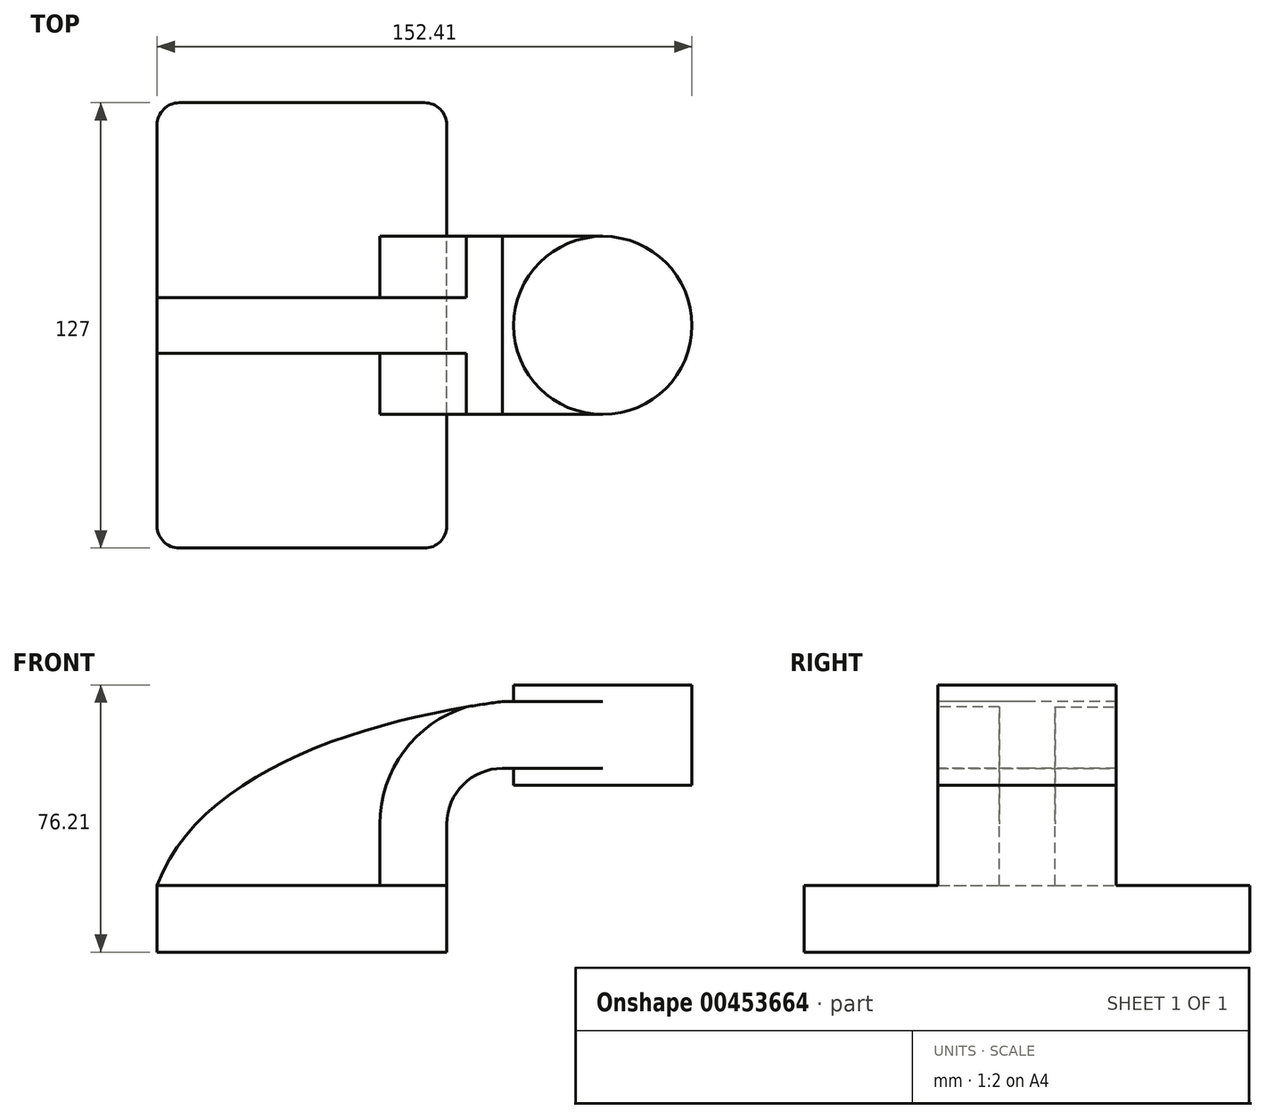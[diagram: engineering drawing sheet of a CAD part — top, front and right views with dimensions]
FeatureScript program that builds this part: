
annotation { "Feature Type Name" : "Feature", "Feature Type Description" : "" }
export const myFeature = defineFeature(function(context is Context, id is Id, definition is map)
    precondition{}
    {
        {
            var Q0;
            Q0=qCreatedBy(makeId("Front.planeOp"),FACE);
            var sketch = newSketch(context, id + "F0", { "sketchPlane" : qUnion([Q0])});
            skLineSegment(sketch, "E0.bottom", {"start": v(41.27, 9.53) * mm, "end": v(-41.28, 9.53) * mm});
            skLineSegment(sketch, "E0.top", {"start": v(41.28, -9.52) * mm, "end": v(-41.27, -9.52) * mm});
            skLineSegment(sketch, "E0.left", {"start": v(41.28, 9.53) * mm, "end": v(41.28, -9.52) * mm});
            skLineSegment(sketch, "E0.right", {"start": v(-41.28, 9.53) * mm, "end": v(-41.27, -9.52) * mm});
            skPoint(sketch, "E0.middle", {"position": v(0, 0) * mm});
            skLineSegment(sketch, "E1.bottom", {"start": v(111.13, 38.1) * mm, "end": v(60.32, 38.1) * mm});
            skLineSegment(sketch, "E1.top", {"start": v(111.13, 66.68) * mm, "end": v(60.33, 66.68) * mm});
            skLineSegment(sketch, "E1.left", {"start": v(111.13, 38.1) * mm, "end": v(111.13, 66.68) * mm});
            skLineSegment(sketch, "E1.right", {"start": v(60.33, 38.1) * mm, "end": v(60.33, 66.68) * mm});
            skPoint(sketch, "E1.middle", {"position": v(85.73, 52.39) * mm});
            skLineSegment(sketch, "E2", {"start": v(41.27, 9.53) * mm, "end": v(41.27, 27) * mm});
            skArc(sketch, "E3", {"start": v(41.27, 27) * mm, "mid": v(45.92, 38.23) * mm, "end": v(57.15, 42.88) * mm});
            skArc(sketch, "E4.1", {"start": v(22.23, 27) * mm, "mid": v(32.45, 51.7) * mm, "end": v(57.15, 61.93) * mm});
            skLineSegment(sketch, "E4.2", {"start": v(22.22, 9.53) * mm, "end": v(22.22, 27) * mm});
            skFitSpline(sketch, "E5", {"points": [v(-41.28, 9.52) * mm, v(57.15, 61.93) * mm], "startDerivative": vector(36.02, 97.65) * mm, "endDerivative": vector(119.13, 15.74) * mm});
            skLineSegment(sketch, "E6", {"start": v(85.73, 38.1) * mm, "end": v(85.73, 66.68) * mm});
            skLineSegment(sketch, "E7", {"start": v(57.15, 61.93) * mm, "end": v(85.73, 61.93) * mm});
            skLineSegment(sketch, "E8", {"start": v(57.15, 42.88) * mm, "end": v(85.73, 42.88) * mm});
            skSolve(sketch);
        }
        {
            var Q0;
            Q0=makeQuery(id+"F0.imprint","IMPRINT",FACE,{"disambiguationData":[TD([[makeQuery(id+"F0.imprint","IMPRINT",EDGE,{"derivedFrom":sQuery(id+"F0.wireOp",EDGE,"E0.top")}),-1.0]])]});
            extrude(context, id + "F1", {"entities" : qUnion([Q0]), "endBound" : BoundingType.SYMMETRIC, "depth" : 127 * mm});
        }
        {
            var Q0;
            {var subQ1=sQuery(id+"F0.wireOp",EDGE,"E2");Q0=makeQuery(id+"F0.imprint","IMPRINT",FACE,{"disambiguationData":[TD([[makeQuery(id+"F0.imprint","IMPRINT",EDGE,{"derivedFrom":subQ1}),1.0]])]});}
            var Q1;
            {var subQ0=sQuery(id+"F0.wireOp",EDGE,"E8");var subQ1=sQuery(id+"F0.wireOp",EDGE,"E1.right");var subQ2=makeQuery(id+"F0.imprint","INTERSECT",VERTEX,{"derivedFrom":[subQ1,subQ0]});Q1=makeQuery(id+"F0.imprint","IMPRINT",FACE,{"disambiguationData":[TD([[makeQuery(id+"F0.imprint","IMPRINT",EDGE,{"disambiguationData":[TD([[subQ2,-1.0]])],"derivedFrom":subQ1}),-1.0]])]});}
            extrude(context, id + "F2", {"entities" : qUnion([Q0, Q1]), "operationType" : NewBodyOperationType.ADD, "endBound" : BoundingType.SYMMETRIC, "depth" : 50.8 * mm});
        }
        {
            var Q0;
            {var subQ3=sQuery(id+"F0.wireOp",EDGE,"E4.2");Q0=makeQuery(id+"F0.imprint","IMPRINT",FACE,{"disambiguationData":[TD([[makeQuery(id+"F0.imprint","IMPRINT",EDGE,{"derivedFrom":subQ3}),1.0]])]});}
            extrude(context, id + "F3", {"entities" : qUnion([Q0]), "operationType" : NewBodyOperationType.ADD, "endBound" : BoundingType.SYMMETRIC, "depth" : 15.88 * mm});
        }
        {
            var Q0;
            {var subQ0=sQuery(id+"F0.wireOp",EDGE,"E1.left");Q0=makeQuery(id+"F0.imprint","IMPRINT",FACE,{"disambiguationData":[TD([[makeQuery(id+"F0.imprint","IMPRINT",EDGE,{"derivedFrom":subQ0}),1.0]])]});}
            var Q1;
            Q1=sQuery(id+"F0.wireOp",EDGE,"E6");
            revolve(context, id + "F4", {"operationType" : NewBodyOperationType.ADD, "entities" : qUnion([Q0]), "axis" : qUnion([Q1]), "revolveType" : RevolveType.FULL});
        }
        {
            var Q0;
            Q0=makeQuery(id+"F1.opExtrude","CAP_EDGE",EDGE,{"disambiguationData":[OSD([sQuery(id+"F0.wireOp",EDGE,"E0.left")])],"isStart":false});
            var Q1;
            Q1=makeQuery(id+"F1.opExtrude","CAP_EDGE",EDGE,{"disambiguationData":[OSD([sQuery(id+"F0.wireOp",EDGE,"E0.left")])],"isStart":true});
            var Q2;
            Q2=makeQuery(id+"F1.opExtrude","CAP_EDGE",EDGE,{"disambiguationData":[OSD([sQuery(id+"F0.wireOp",EDGE,"E0.right")])],"isStart":true});
            var Q3;
            Q3=makeQuery(id+"F1.opExtrude","CAP_EDGE",EDGE,{"disambiguationData":[OSD([sQuery(id+"F0.wireOp",EDGE,"E0.right")])],"isStart":false});
            fillet(context, id + "F5", {"entities" : qUnion([Q0, Q1, Q2, Q3]), "radius" : 6.35 * mm, "tangentPropagation" : true, "allowEdgeOverflow" : false});
        }
    });
